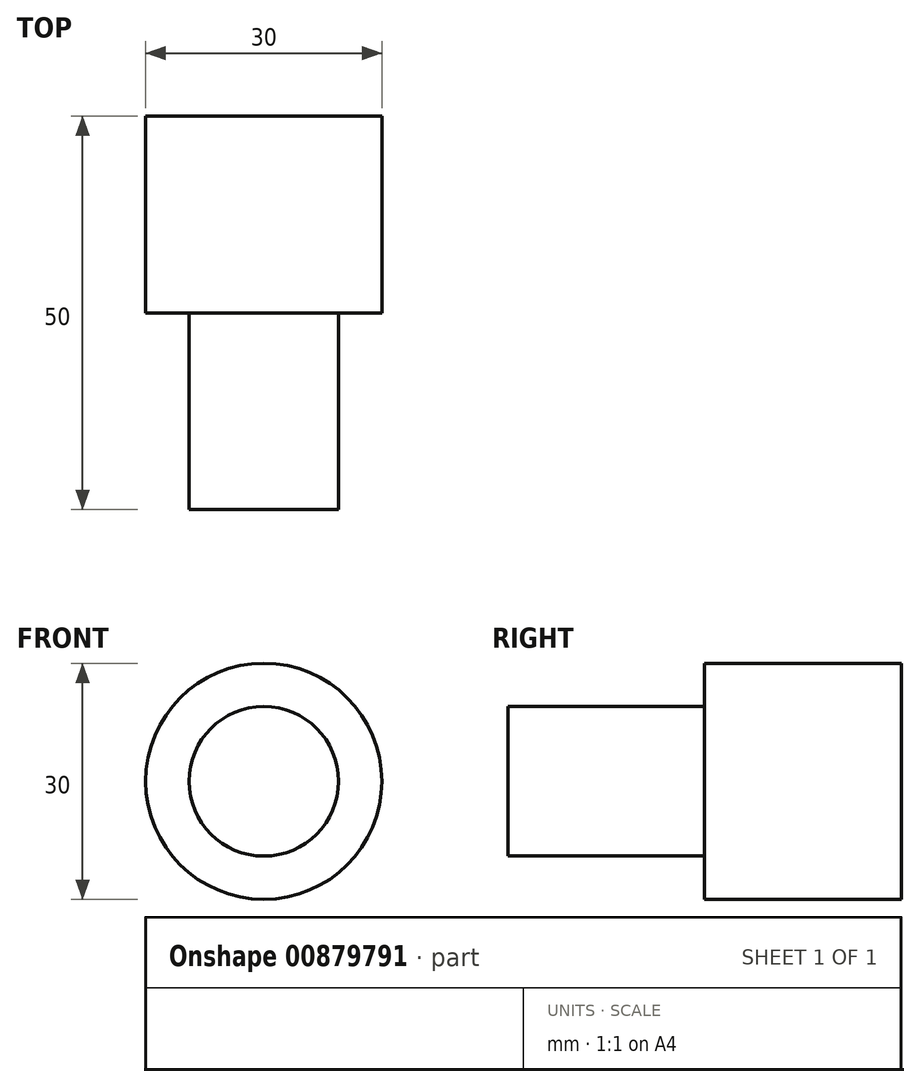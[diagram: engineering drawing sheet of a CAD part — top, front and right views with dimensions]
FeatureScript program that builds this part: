
annotation { "Feature Type Name" : "Feature", "Feature Type Description" : "" }
export const myFeature = defineFeature(function(context is Context, id is Id, definition is map)
    precondition{}
    {
        {
            var Q0;
            Q0=qCreatedBy(makeId("Front.planeOp"),FACE);
            var sketch = newSketch(context, id + "F0", { "sketchPlane" : qUnion([Q0])});
            skCircle(sketch, "E0", {"center": v(0, 0) * mm, "radius": 9.5 * mm});
            skSolve(sketch);
        }
        {
            var Q0;
            Q0=makeQuery(id+"F0.imprint","IMPRINT",FACE,{"disambiguationData":[TD([[makeQuery(id+"F0.imprint","IMPRINT",EDGE,{"derivedFrom":sQuery(id+"F0.wireOp",EDGE,"E0")}),1.0]])]});
            extrude(context, id + "F1", {"entities" : qUnion([Q0]), "oppositeDirection" : true, "depth" : 25 * mm, "offsetDistance" : 25 * mm});
        }
        {
            var Q0;
            Q0=makeQuery(id+"F1.opExtrude","CAP_FACE",FACE,{"disambiguationData":[OSD([sQuery(id+"F0.wireOp",EDGE,"E0")])],"isStart":false});
            var sketch = newSketch(context, id + "F2", { "sketchPlane" : qUnion([Q0])});
            skCircle(sketch, "E1", {"center": v(0, 0) * mm, "radius": 15 * mm});
            skSolve(sketch);
        }
        {
            var Q0;
            Q0=makeQuery(id+"F2.imprint","IMPRINT",FACE,{"disambiguationData":[TD([[makeQuery(id+"F2.imprint","IMPRINT",EDGE,{"derivedFrom":makeQuery(id+"F1.opExtrude","CAP_EDGE",EDGE,{"disambiguationData":[OSD([sQuery(id+"F0.wireOp",EDGE,"E0")])],"isStart":false})}),-1.0]])]});
            var Q1;
            Q1=makeQuery(id+"F2.imprint","IMPRINT",FACE,{"disambiguationData":[TD([[makeQuery(id+"F2.imprint","IMPRINT",EDGE,{"derivedFrom":sQuery(id+"F2.wireOp",EDGE,"E1")}),1.0]])]});
            extrude(context, id + "F3", {"entities" : qUnion([Q0, Q1]), "operationType" : NewBodyOperationType.ADD, "depth" : 25 * mm, "offsetDistance" : 25 * mm});
        }
    });
